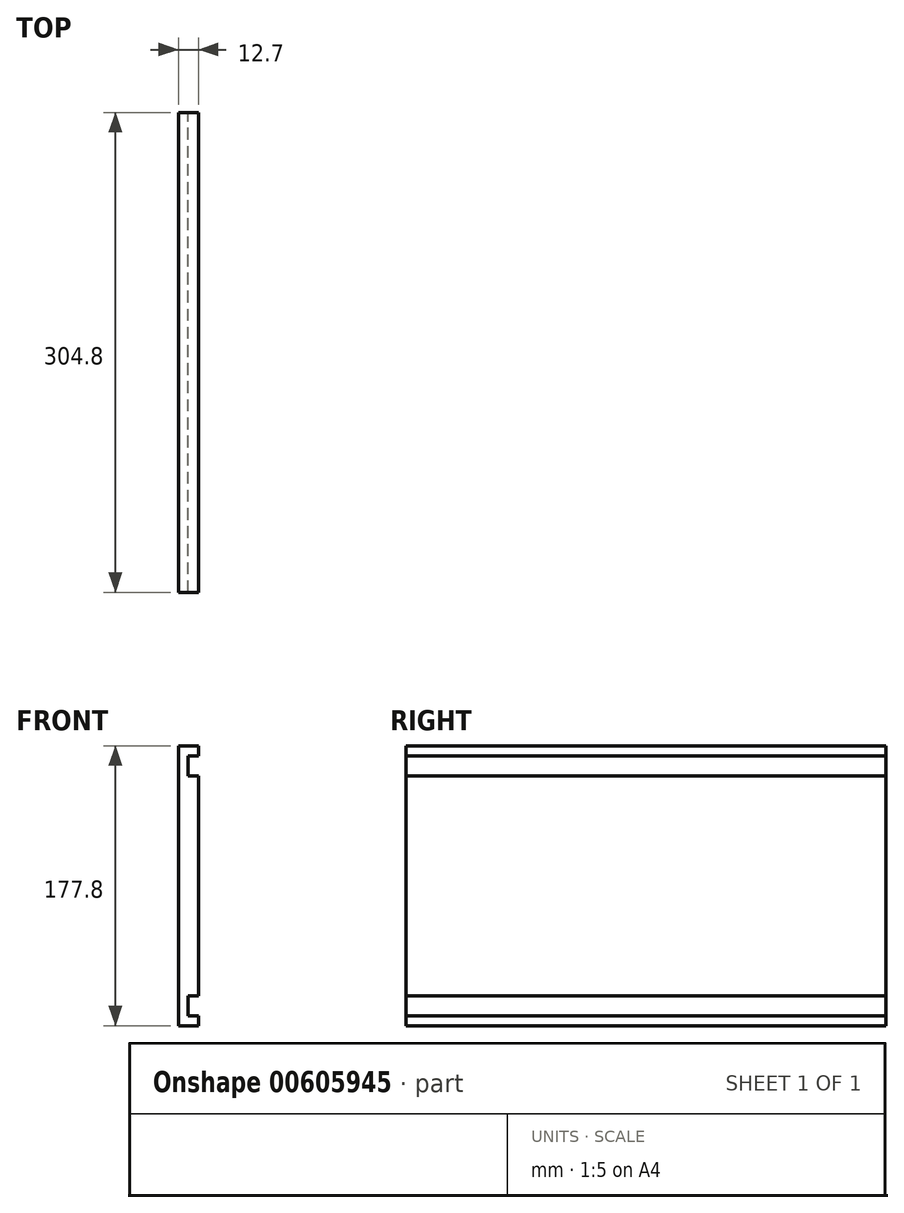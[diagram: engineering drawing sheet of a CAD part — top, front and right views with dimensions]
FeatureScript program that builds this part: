
annotation { "Feature Type Name" : "Feature", "Feature Type Description" : "" }
export const myFeature = defineFeature(function(context is Context, id is Id, definition is map)
    precondition{}
    {
        {
            var Q0;
            Q0=qCreatedBy(makeId("Right.planeOp"),FACE);
            var sketch = newSketch(context, id + "F0", { "sketchPlane" : qUnion([Q0])});
            skLineSegment(sketch, "E0.bottom", {"start": v(0, 0) * mm, "end": v(304.8, 0) * mm});
            skLineSegment(sketch, "E0.top", {"start": v(0, 177.8) * mm, "end": v(304.8, 177.8) * mm});
            skLineSegment(sketch, "E0.left", {"start": v(0, 0) * mm, "end": v(0, 177.8) * mm});
            skLineSegment(sketch, "E0.right", {"start": v(304.8, 0) * mm, "end": v(304.8, 177.8) * mm});
            skSolve(sketch);
        }
        {
            var Q0;
            Q0=makeQuery(id+"F0.imprint","IMPRINT",FACE,{"disambiguationData":[TD([[makeQuery(id+"F0.imprint","IMPRINT",EDGE,{"derivedFrom":sQuery(id+"F0.wireOp",EDGE,"E0.bottom")}),1.0]])]});
            extrude(context, id + "F1", {"entities" : qUnion([Q0]), "depth" : 12.7 * mm, "offsetDistance" : 25.4 * mm});
        }
        {
            var Q0;
            Q0=makeQuery(id+"F1.opExtrude","CAP_FACE",FACE,{"disambiguationData":[OSD([sQuery(id+"F0.wireOp",EDGE,"E0.bottom"),sQuery(id+"F0.wireOp",EDGE,"E0.top"),sQuery(id+"F0.wireOp",EDGE,"E0.left"),sQuery(id+"F0.wireOp",EDGE,"E0.right")])],"isStart":false});
            var sketch = newSketch(context, id + "F2", { "sketchPlane" : qUnion([Q0])});
            skLineSegment(sketch, "E1", {"start": v(0, 0) * mm, "end": v(0, 6.35) * mm});
            skLineSegment(sketch, "E2", {"start": v(0, 6.35) * mm, "end": v(0, 19.05) * mm});
            skLineSegment(sketch, "E3", {"start": v(0, 19.05) * mm, "end": v(304.8, 19.05) * mm});
            skLineSegment(sketch, "E4", {"start": v(304.8, 19.05) * mm, "end": v(304.8, 6.35) * mm});
            skLineSegment(sketch, "E5", {"start": v(0, 6.35) * mm, "end": v(304.8, 6.35) * mm});
            skSolve(sketch);
        }
        {
            var Q0;
            Q0=makeQuery(id+"F2.imprint","IMPRINT",FACE,{"disambiguationData":[TD([[makeQuery(id+"F2.imprint","IMPRINT",EDGE,{"derivedFrom":sQuery(id+"F2.wireOp",EDGE,"E2")}),-1.0]])]});
            extrude(context, id + "F3", {"entities" : qUnion([Q0]), "operationType" : NewBodyOperationType.REMOVE, "oppositeDirection" : true, "depth" : 6.35 * mm, "offsetDistance" : 25.4 * mm});
        }
        {
            var Q0;
            {var subQ0=sQuery(id+"F0.wireOp",EDGE,"E0.top");var subQ1=sQuery(id+"F0.wireOp",EDGE,"E0.left");var subQ2=sQuery(id+"F0.wireOp",EDGE,"E0.right");Q0=makeQuery(id+"F3.boolean.opBoolean","SPLIT",FACE,{"disambiguationData":[TD([makeQuery(id+"F1.opExtrude","SWEPT_FACE",FACE,{"disambiguationData":[OSD([subQ0])]})])],"derivedFrom":makeQuery(id+"F1.opExtrude","CAP_FACE",FACE,{"disambiguationData":[OSD([sQuery(id+"F0.wireOp",EDGE,"E0.bottom"),subQ0,subQ1,subQ2])],"isStart":false})});}
            var sketch = newSketch(context, id + "F4", { "sketchPlane" : qUnion([Q0])});
            skLineSegment(sketch, "E6", {"start": v(0, 177.8) * mm, "end": v(0, 171.45) * mm});
            skLineSegment(sketch, "E7", {"start": v(0, 171.45) * mm, "end": v(0, 158.75) * mm});
            skLineSegment(sketch, "E8", {"start": v(0, 158.75) * mm, "end": v(304.8, 158.75) * mm});
            skLineSegment(sketch, "E9", {"start": v(304.8, 158.75) * mm, "end": v(304.8, 171.45) * mm});
            skLineSegment(sketch, "E10", {"start": v(304.8, 171.45) * mm, "end": v(0, 171.45) * mm});
            skSolve(sketch);
        }
        {
            var Q0;
            Q0=makeQuery(id+"F4.imprint","IMPRINT",FACE,{"disambiguationData":[TD([[makeQuery(id+"F4.imprint","IMPRINT",EDGE,{"derivedFrom":sQuery(id+"F4.wireOp",EDGE,"E7")}),-1.0]])]});
            extrude(context, id + "F5", {"entities" : qUnion([Q0]), "operationType" : NewBodyOperationType.REMOVE, "oppositeDirection" : true, "depth" : 6.35 * mm, "offsetDistance" : 25.4 * mm});
        }
    });
